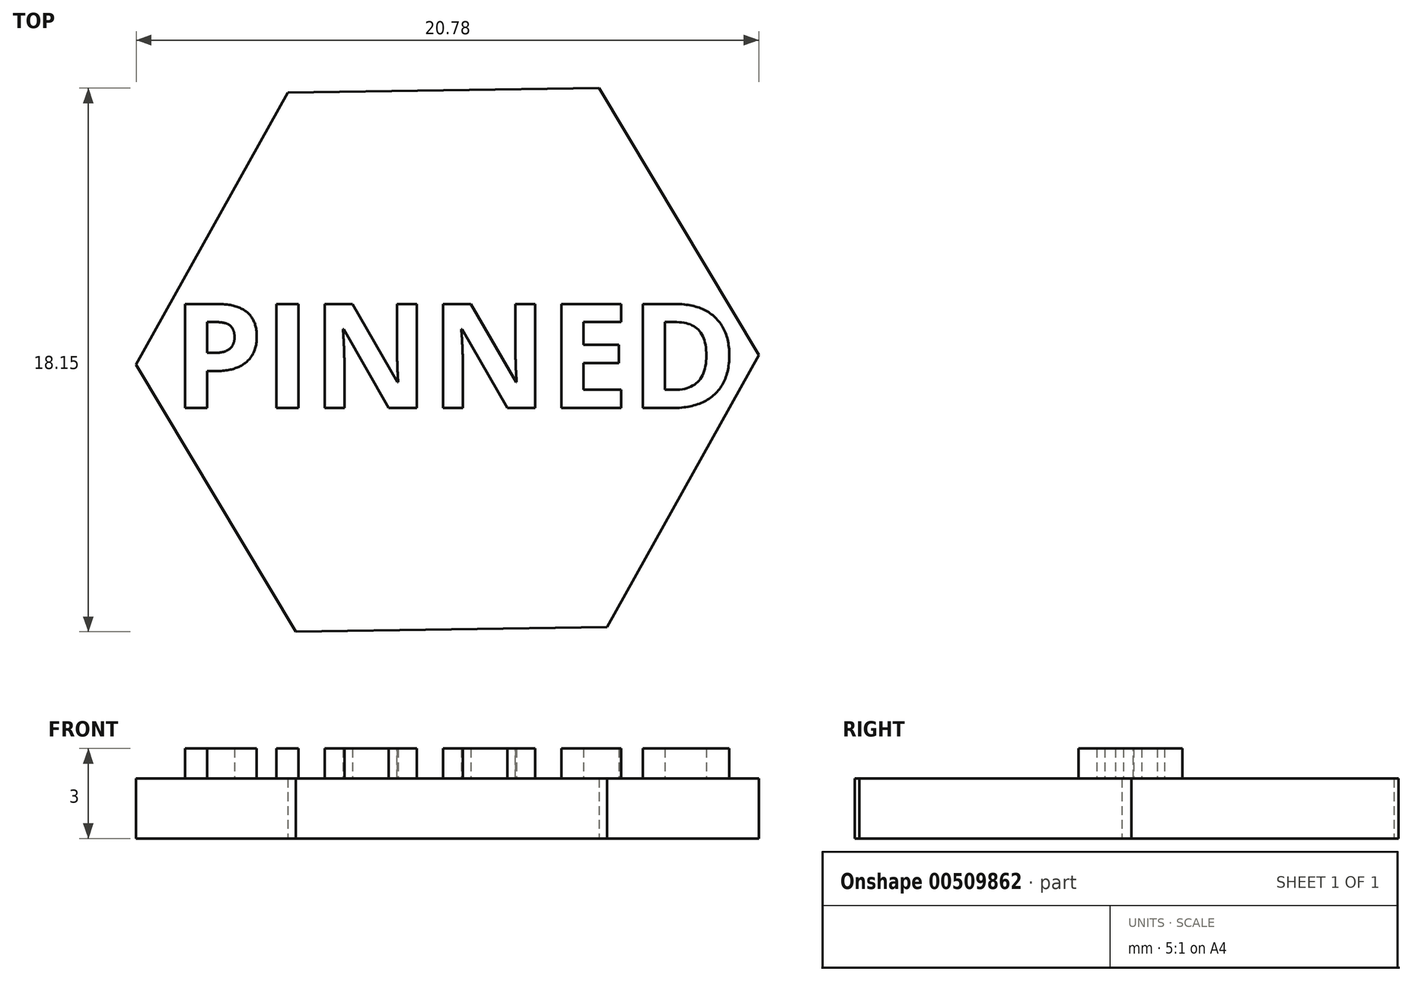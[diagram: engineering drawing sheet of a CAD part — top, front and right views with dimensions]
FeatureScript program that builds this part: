
annotation { "Feature Type Name" : "Feature", "Feature Type Description" : "" }
export const myFeature = defineFeature(function(context is Context, id is Id, definition is map)
    precondition{}
    {
        {
            var Q0;
            Q0=qCreatedBy(makeId("Top.planeOp"),FACE);
            var sketch = newSketch(context, id + "F0", { "sketchPlane" : qUnion([Q0])});
            skCircle(sketch, "E0.cCircle", {"center": v(-21.24, 31.76) * mm, "radius": 9 * mm, "construction": true});
            skLineSegment(sketch, "E0.0", {"start": v(-10.85, 31.91) * mm, "end": v(-15.91, 22.83) * mm});
            skLineSegment(sketch, "E0.1", {"start": v(-15.91, 22.83) * mm, "end": v(-26.3, 22.68) * mm});
            skLineSegment(sketch, "E0.2", {"start": v(-26.3, 22.68) * mm, "end": v(-31.63, 31.6) * mm});
            skLineSegment(sketch, "E0.3", {"start": v(-31.63, 31.6) * mm, "end": v(-26.57, 40.68) * mm});
            skLineSegment(sketch, "E0.4", {"start": v(-26.57, 40.68) * mm, "end": v(-16.18, 40.83) * mm});
            skLineSegment(sketch, "E0.5", {"start": v(-16.18, 40.83) * mm, "end": v(-10.85, 31.91) * mm});
            skPoint(sketch, "E0.0.midPoint", {"position": v(-13.38, 27.37) * mm});
            skSolve(sketch);
        }
        {
            var Q0;
            Q0=qSketchRegion(id+"F0",true);
            extrude(context, id + "F1", {"entities" : qUnion([Q0]), "depth" : 2 * mm, "offsetDistance" : 25 * mm});
        }
        {
            var Q0;
            Q0=makeQuery(id+"F1.opExtrude","CAP_FACE",FACE,{"disambiguationData":[OSD([sQuery(id+"F0.wireOp",EDGE,"E0.0"),sQuery(id+"F0.wireOp",EDGE,"E0.1"),sQuery(id+"F0.wireOp",EDGE,"E0.2"),sQuery(id+"F0.wireOp",EDGE,"E0.3"),sQuery(id+"F0.wireOp",EDGE,"E0.4"),sQuery(id+"F0.wireOp",EDGE,"E0.5")])],"isStart":false});
            var sketch = newSketch(context, id + "F2", { "sketchPlane" : qUnion([Q0])});
            skText(sketch, "E1", { "text": "PINNED", "fontName": "OpenSans-Bold.ttf"});
            const initialGuessF2  = {"E1": [-0.03044, 0.03015, 1, 0, 0.0035]};
            skSetInitialGuess(sketch, initialGuessF2);
            skSolve(sketch);
        }
        {
            var Q0;
            Q0 = qSketchRegion(id + "F2", true);
            extrude(context, id + "F3", {"entities" : qUnion([Q0]), "operationType" : NewBodyOperationType.ADD, "depth" : 1 * mm, "offsetDistance" : 25 * mm});
        }
    });
